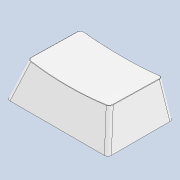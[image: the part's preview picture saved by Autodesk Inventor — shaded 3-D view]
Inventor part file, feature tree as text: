
AUTODESK INVENTOR PART (.ipt)
format: ipt  version: 2021 (Build 250183000, 183)  size: 235,008 bytes
history: native  units: in
note: dims shown in document units (in); Inventor stores cm internally (conversion verified against a paired STEP export)
features: chamfer x1
ambient origin geometry x8: Origin, YZ Plane, XZ Plane, XY Plane, X Axis, Y Axis, Z Axis, Center Point
bodies: Solid1 (feature_tree)
feature tree (1):
  chamfer  "Chamfer1"  [1 undecoded]
note: 1 required parameter value undecoded (feature->parameter linkage not recoverable at this tier; creation-order binding heuristic only, values carry confidence <= 0.55)
